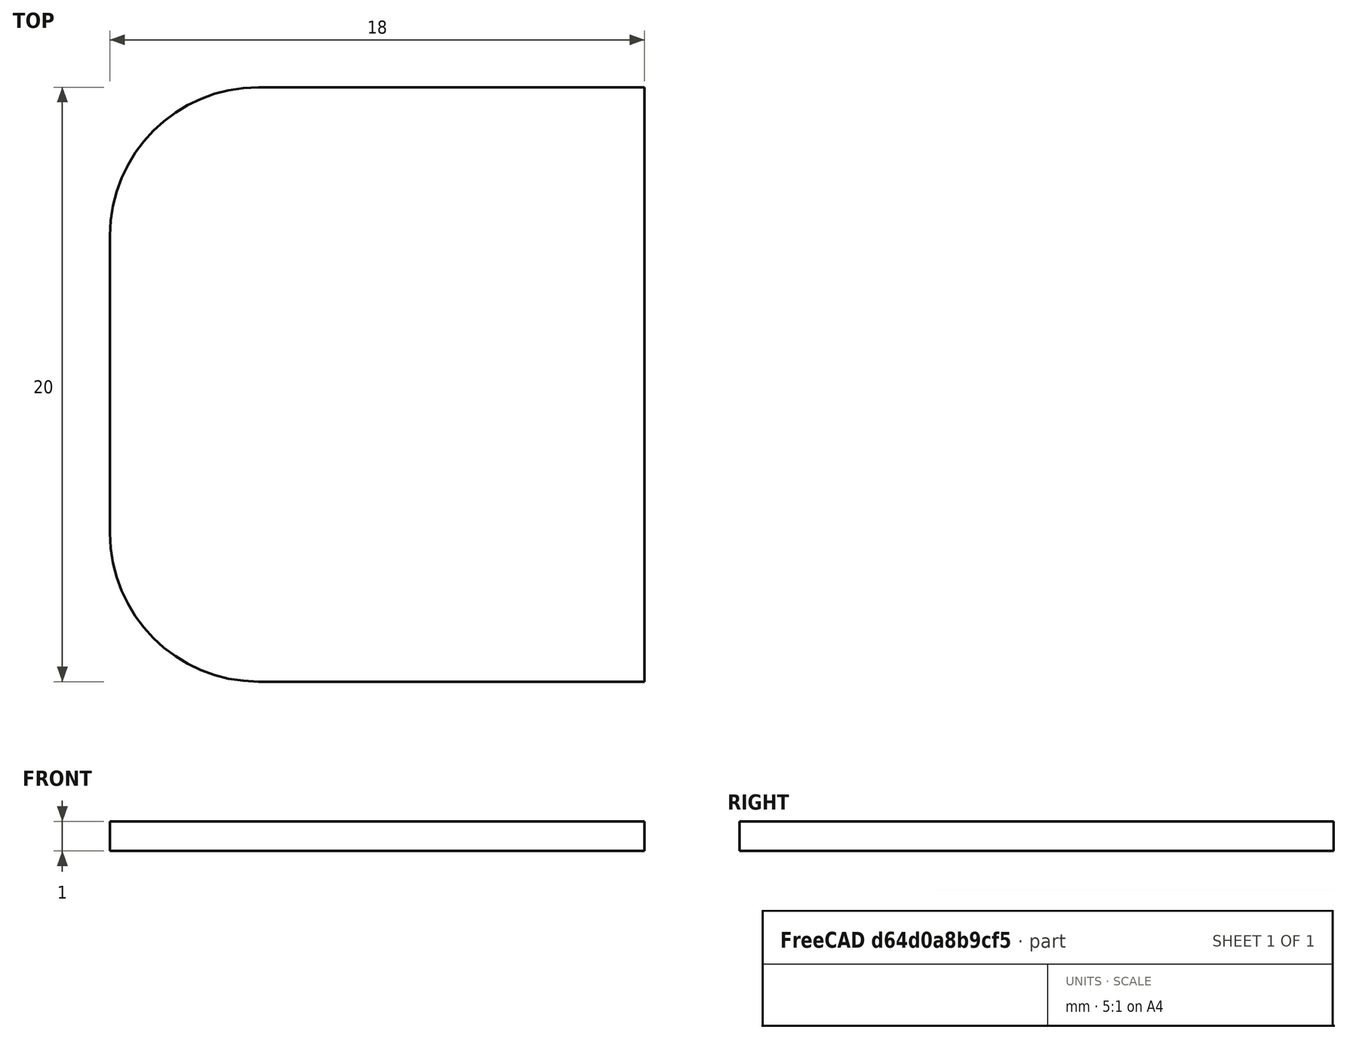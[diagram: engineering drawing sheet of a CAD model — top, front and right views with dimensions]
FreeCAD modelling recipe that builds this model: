
FCSTD DOCUMENT  (FreeCAD 0.17R13528 (Git))
Label: NutriExplainerEdge
License: All rights reserved
LicenseURL: http://en.wikipedia.org/wiki/All_rights_reserved
objects: Sketcher::SketchObject×1, PartDesign::Pad×1, PartDesign::Body×1
note: 4 computed .brp shape members not serialized (recipe doc carries the construction recipe); baked Part::Feature solids carry a one-line shape summary decoded from their .brp

FEATURE [Sketcher::SketchObject] Sketch
  MapMode = 5
  Support = -> [XY_Plane]
  sketch-geometry (6):
    g0: LineSegment StartX=-4 StartY=10 StartZ=0 EndX=9 EndY=10 EndZ=0
    g1: LineSegment StartX=9 StartY=10 StartZ=0 EndX=9 EndY=-10 EndZ=0
    g2: LineSegment StartX=9 StartY=-10 StartZ=0 EndX=-4 EndY=-10 EndZ=0
    g3: LineSegment StartX=-9 StartY=-5 StartZ=0 EndX=-9 EndY=5 EndZ=0
    g4: ArcOfCircle CenterX=-4 CenterY=5 CenterZ=0 NormalX=0 NormalY=0 NormalZ=1 AngleXU=0 Radius=5 StartAngle=1.5708 EndAngle=3.14159
    g5: ArcOfCircle CenterX=-4 CenterY=-5 CenterZ=0 NormalX=0 NormalY=0 NormalZ=1 AngleXU=0 Radius=5 StartAngle=3.14159 EndAngle=4.71239
  constraints (16):
    c: Coincident(g0,g1)
    c: Coincident(g1,g2)
    c: Horizontal(g0)
    c: Horizontal(g2)
    c: Vertical(g1)
    c: Vertical(g3)
    c: DistanceY(g1,g1) = 20
    c: Tangent(g3,g4) = 1.5708
    c: Tangent(g0,g4) = 1.5708
    c: Tangent(g3,g5) = 1.5708
    c: Tangent(g2,g5) = 1.5708
    c: DistanceX(g3,g0) = 18
    c: DistanceX(g-1,g3) = -9
    c: Equal(g4,g5)
    c: Radius(g5) = 5
    c: DistanceY(g2,g-1) = 10
FEATURE [PartDesign::Pad] Pad
  Length = 1
  Length2 = 100
  Profile = -> Sketch
  Type = 0
FEATURE [PartDesign::Body] Body
  Group = -> [Sketch,Pad]
  Origin = -> Origin
  Tip = -> Pad
